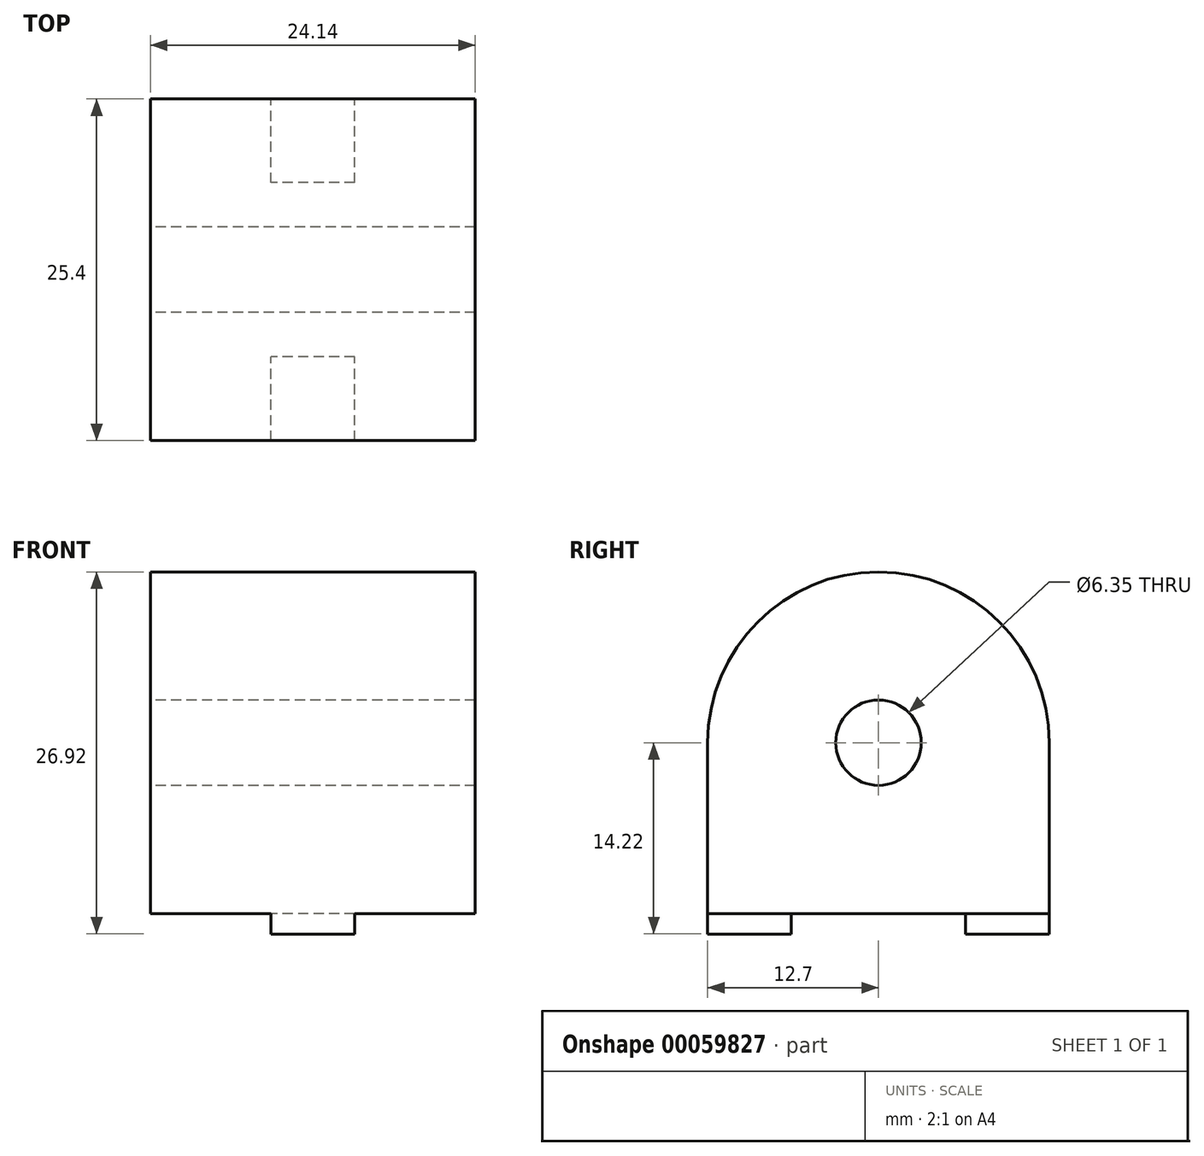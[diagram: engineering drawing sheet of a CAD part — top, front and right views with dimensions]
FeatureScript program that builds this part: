
annotation { "Feature Type Name" : "Feature", "Feature Type Description" : "" }
export const myFeature = defineFeature(function(context is Context, id is Id, definition is map)
    precondition{}
    {
        {
            var Q0;
            Q0=qCreatedBy(makeId("Right.planeOp"),FACE);
            var sketch = newSketch(context, id + "F0", { "sketchPlane" : qUnion([Q0])});
            skLineSegment(sketch, "E0.bottom", {"start": v(-12.7, 12.7) * mm, "end": v(12.7, 12.7) * mm});
            skLineSegment(sketch, "E0.top", {"start": v(-12.7, 0) * mm, "end": v(12.7, 0) * mm});
            skLineSegment(sketch, "E0.left", {"start": v(-12.7, 12.7) * mm, "end": v(-12.7, 0) * mm});
            skLineSegment(sketch, "E0.right", {"start": v(12.7, 12.7) * mm, "end": v(12.7, 0) * mm});
            skArc(sketch, "E1", {"start": v(12.7, 12.7) * mm, "mid": v(0, 25.4) * mm, "end": v(-12.7, 12.7) * mm});
            skCircle(sketch, "E2", {"center": v(0, 12.7) * mm, "radius": 3.18 * mm});
            skSolve(sketch);
        }
        {
            var Q0;
            Q0 = qSketchRegion(id + "F0", true);
            extrude(context, id + "F1", {"entities" : qUnion([Q0]), "depth" : 24.13 * mm, "symmetric" : true});
        }
        {
            var Q0;
            Q0=qCreatedBy(makeId("Front.planeOp"),FACE);
            var sketch = newSketch(context, id + "F2", { "sketchPlane" : qUnion([Q0])});
            skLineSegment(sketch, "E3.bottom", {"start": v(-3.11, 0) * mm, "end": v(3.11, 0) * mm});
            skLineSegment(sketch, "E3.top", {"start": v(-3.11, -1.52) * mm, "end": v(3.11, -1.52) * mm});
            skLineSegment(sketch, "E3.left", {"start": v(-3.11, 0) * mm, "end": v(-3.11, -1.52) * mm});
            skLineSegment(sketch, "E3.right", {"start": v(3.11, 0) * mm, "end": v(3.11, -1.52) * mm});
            skSolve(sketch);
        }
        {
            var Q0;
            Q0 = qSketchRegion(id + "F2", true);
            var Q1;
            Q1=makeQuery(id+"F1.opExtrude","SWEPT_FACE",FACE,{"disambiguationData":[OSD([sQuery(id+"F0.wireOp",EDGE,"E0.left")])]});
            var Q2;
            Q2=makeQuery(id+"F1.opExtrude","SWEPT_FACE",FACE,{"disambiguationData":[OSD([sQuery(id+"F0.wireOp",EDGE,"E0.right")])]});
            extrude(context, id + "F3", {"entities" : qUnion([Q0]), "operationType" : NewBodyOperationType.ADD, "endBound" : BoundingType.UP_TO_SURFACE, "endBoundEntityFace" : qUnion([Q1]), "depth" : 25.4 * mm, "hasSecondDirection" : true, "secondDirectionBound" : BoundingType.UP_TO_SURFACE, "secondDirectionOppositeDirection" : true, "secondDirectionBoundEntityFace" : qUnion([Q2]), "secondDirectionDepth" : 25.4 * mm});
        }
        {
            var Q0;
            Q0=makeQuery(id+"F3.opExtrude","SWEPT_FACE",FACE,{"disambiguationData":[OSD([sQuery(id+"F2.wireOp",EDGE,"E3.left")])]});
            var sketch = newSketch(context, id + "F4", { "sketchPlane" : qUnion([Q0])});
            skLineSegment(sketch, "E4.bottom", {"start": v(-6.48, -1.52) * mm, "end": v(6.48, -1.52) * mm});
            skLineSegment(sketch, "E4.top", {"start": v(-6.48, 0) * mm, "end": v(6.48, 0) * mm});
            skLineSegment(sketch, "E4.left", {"start": v(-6.48, -1.52) * mm, "end": v(-6.48, 0) * mm});
            skLineSegment(sketch, "E4.right", {"start": v(6.48, -1.52) * mm, "end": v(6.48, 0) * mm});
            skSolve(sketch);
        }
        {
            var Q0;
            Q0 = qSketchRegion(id + "F4", true);
            extrude(context, id + "F5", {"entities" : qUnion([Q0]), "operationType" : NewBodyOperationType.REMOVE, "endBound" : BoundingType.UP_TO_NEXT, "oppositeDirection" : true, "depth" : 25.4 * mm});
        }
    });
